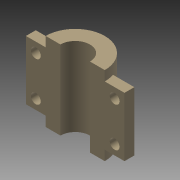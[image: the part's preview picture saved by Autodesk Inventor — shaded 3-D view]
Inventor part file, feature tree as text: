
AUTODESK INVENTOR PART (.ipt)
format: ipt  version: 2015 (Build 190159000, 159)  size: 150,016 bytes
history: native  units: mm
features: extrude x3, sketch x3, pattern_linear x1, fillet x1
ambient origin geometry x8: Origin, YZ Plane, XZ Plane, XY Plane, X Axis, Y Axis, Z Axis, Center Point
bodies: 实体1 (feature_tree)
feature tree (8):
  extrude  "拉伸1"  Depth=30.0mm
  extrude  "拉伸2"  Depth=50.0mm
  pattern_linear  "矩形阵列1"  Spacing1=2.004554mm  [1 undecoded]
  fillet  "圆角1"  Radius=40.0mm
  extrude  "拉伸3"  Depth=5.0mm TaperAngle=0.0deg
  sketch  "草图1"  dims[d0=15.0mm d1=30.0mm]
  sketch  "草图2"  dims[d2=5.0mm d3=50.0mm]
  sketch  "草图3"  dims[d4=4.040926mm d5=2.004554mm d6=40.0mm d7=0.0mm d8=5.0mm d9=0.0mm d10=20.0mm d12=35.0mm d13=0.25mm d14=5.0mm d15=5.0mm d16=5.0mm d17=5.0mm d18=5.0mm d19=5.0mm d20=5.0mm d21=5.0mm d22=5.0mm d23=5.0mm d24=5.0mm d25=5.0mm d26=5.0mm d27=0.0mm]
note: 1 required parameter value undecoded (feature->parameter linkage not recoverable at this tier; creation-order binding heuristic only, values carry confidence <= 0.55)
